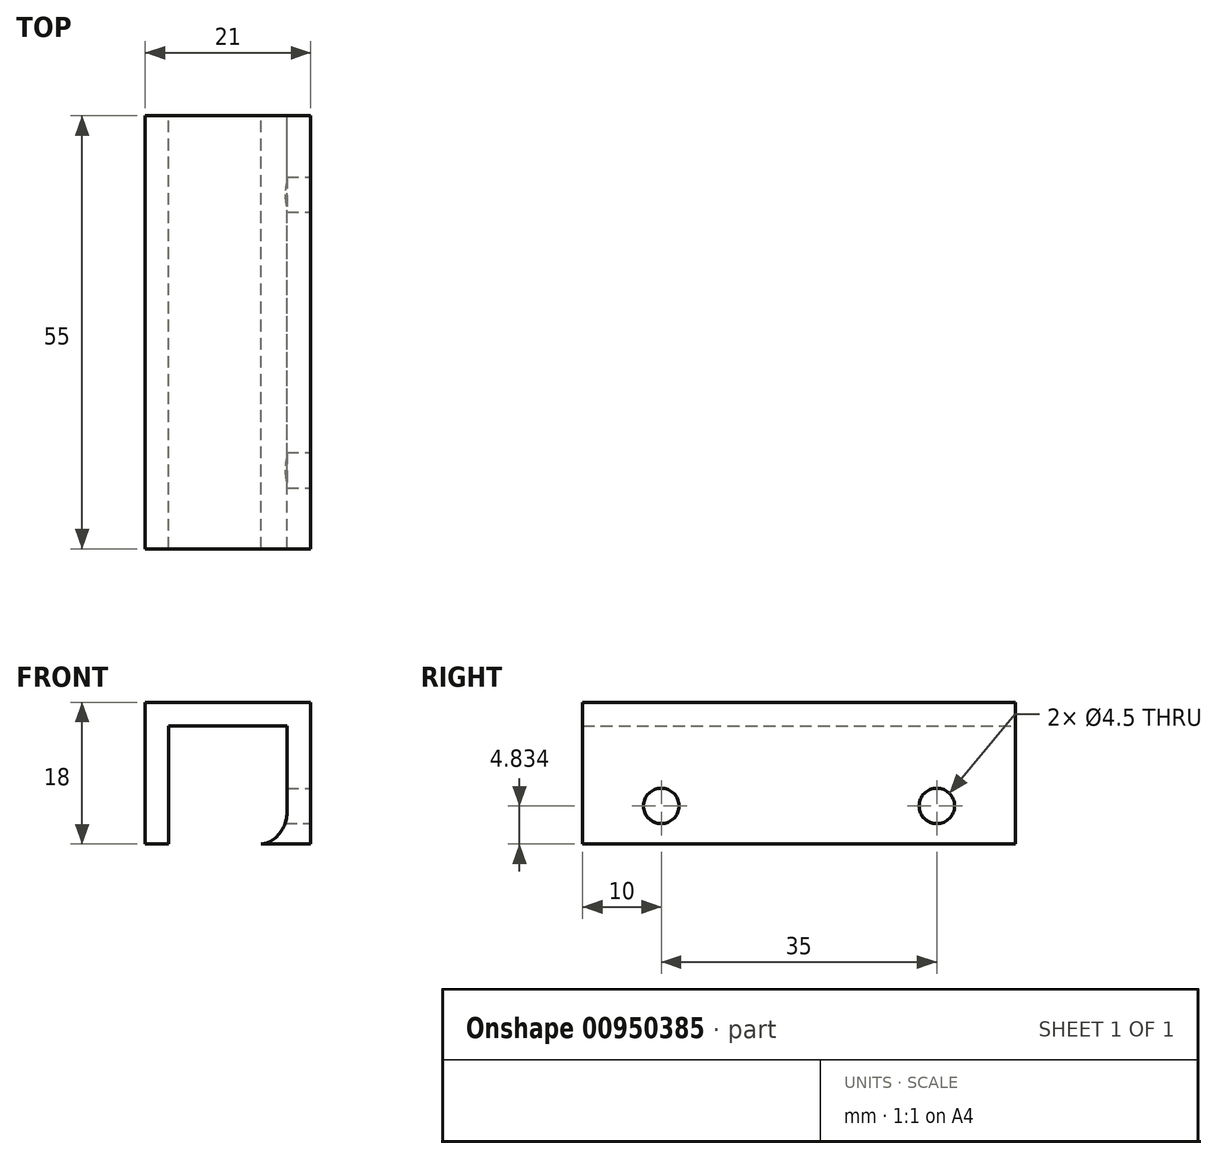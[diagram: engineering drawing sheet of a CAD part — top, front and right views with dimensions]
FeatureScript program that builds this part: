
annotation { "Feature Type Name" : "Feature", "Feature Type Description" : "" }
export const myFeature = defineFeature(function(context is Context, id is Id, definition is map)
    precondition{}
    {
        {
            var Q0;
            Q0=qCreatedBy(makeId("Front.planeOp"),FACE);
            var sketch = newSketch(context, id + "F0", { "sketchPlane" : qUnion([Q0])});
            skLineSegment(sketch, "E0", {"start": v(-5.75, 0) * mm, "end": v(-5.75, 15) * mm});
            skLineSegment(sketch, "E1", {"start": v(-5.75, 15) * mm, "end": v(9.25, 15) * mm});
            skLineSegment(sketch, "E2", {"start": v(9.25, 15) * mm, "end": v(9.25, 3.74) * mm});
            skLineSegment(sketch, "E3", {"start": v(9.25, 0) * mm, "end": v(12.25, 0) * mm});
            skLineSegment(sketch, "E4", {"start": v(12.25, 0) * mm, "end": v(12.25, 18) * mm});
            skLineSegment(sketch, "E5", {"start": v(12.25, 18) * mm, "end": v(-8.75, 18) * mm});
            skLineSegment(sketch, "E6", {"start": v(-8.75, 18) * mm, "end": v(-8.75, 0) * mm});
            skLineSegment(sketch, "E7", {"start": v(-8.75, 0) * mm, "end": v(-5.75, 0) * mm});
            skLineSegment(sketch, "E8", {"start": v(6, 0) * mm, "end": v(9.25, 0) * mm});
            skFitSpline(sketch, "E9", {"points": [v(6, 0) * mm, v(9.25, 3.74) * mm], "startDerivative": vector(4.89, 0) * mm, "endDerivative": vector(0, 5.1) * mm});
            skSolve(sketch);
        }
        {
            var Q0;
            Q0=makeQuery(id+"F0.imprint","IMPRINT",FACE,{"disambiguationData":[TD([[makeQuery(id+"F0.imprint","IMPRINT",EDGE,{"derivedFrom":sQuery(id+"F0.wireOp",EDGE,"E0")}),1.0]])]});
            extrude(context, id + "F1", {"entities" : qUnion([Q0]), "endBound" : BoundingType.SYMMETRIC, "depth" : 55 * mm, "offsetDistance" : 25 * mm});
        }
        {
            var Q0;
            Q0=makeQuery(id+"F1.opExtrude","SWEPT_FACE",FACE,{"disambiguationData":[OSD([sQuery(id+"F0.wireOp",EDGE,"E4")])]});
            var sketch = newSketch(context, id + "F2", { "sketchPlane" : qUnion([Q0])});
            skLineSegment(sketch, "E10", {"start": v(0, 18) * mm, "end": v(0, 0) * mm});
            skCircle(sketch, "E11", {"center": v(-17.5, 4.83) * mm, "radius": 2.25 * mm});
            skCircle(sketch, "E12", {"center": v(17.5, 4.83) * mm, "radius": 2.25 * mm});
            skLineSegment(sketch, "E13", {"start": v(-27.5, 4.83) * mm, "end": v(27.5, 4.83) * mm, "construction": true});
            skSolve(sketch);
        }
        {
            var Q0;
            Q0=makeQuery(id+"F2.imprint","IMPRINT",FACE,{"disambiguationData":[TD([[makeQuery(id+"F2.imprint","IMPRINT",EDGE,{"derivedFrom":sQuery(id+"F2.wireOp",EDGE,"E11")}),1.0]])]});
            var Q1;
            Q1=makeQuery(id+"F2.imprint","IMPRINT",FACE,{"disambiguationData":[TD([[makeQuery(id+"F2.imprint","IMPRINT",EDGE,{"derivedFrom":sQuery(id+"F2.wireOp",EDGE,"E12")}),1.0]])]});
            extrude(context, id + "F3", {"entities" : qUnion([Q0, Q1]), "operationType" : NewBodyOperationType.REMOVE, "oppositeDirection" : true, "depth" : 5 * mm, "offsetDistance" : 25 * mm});
        }
    });
